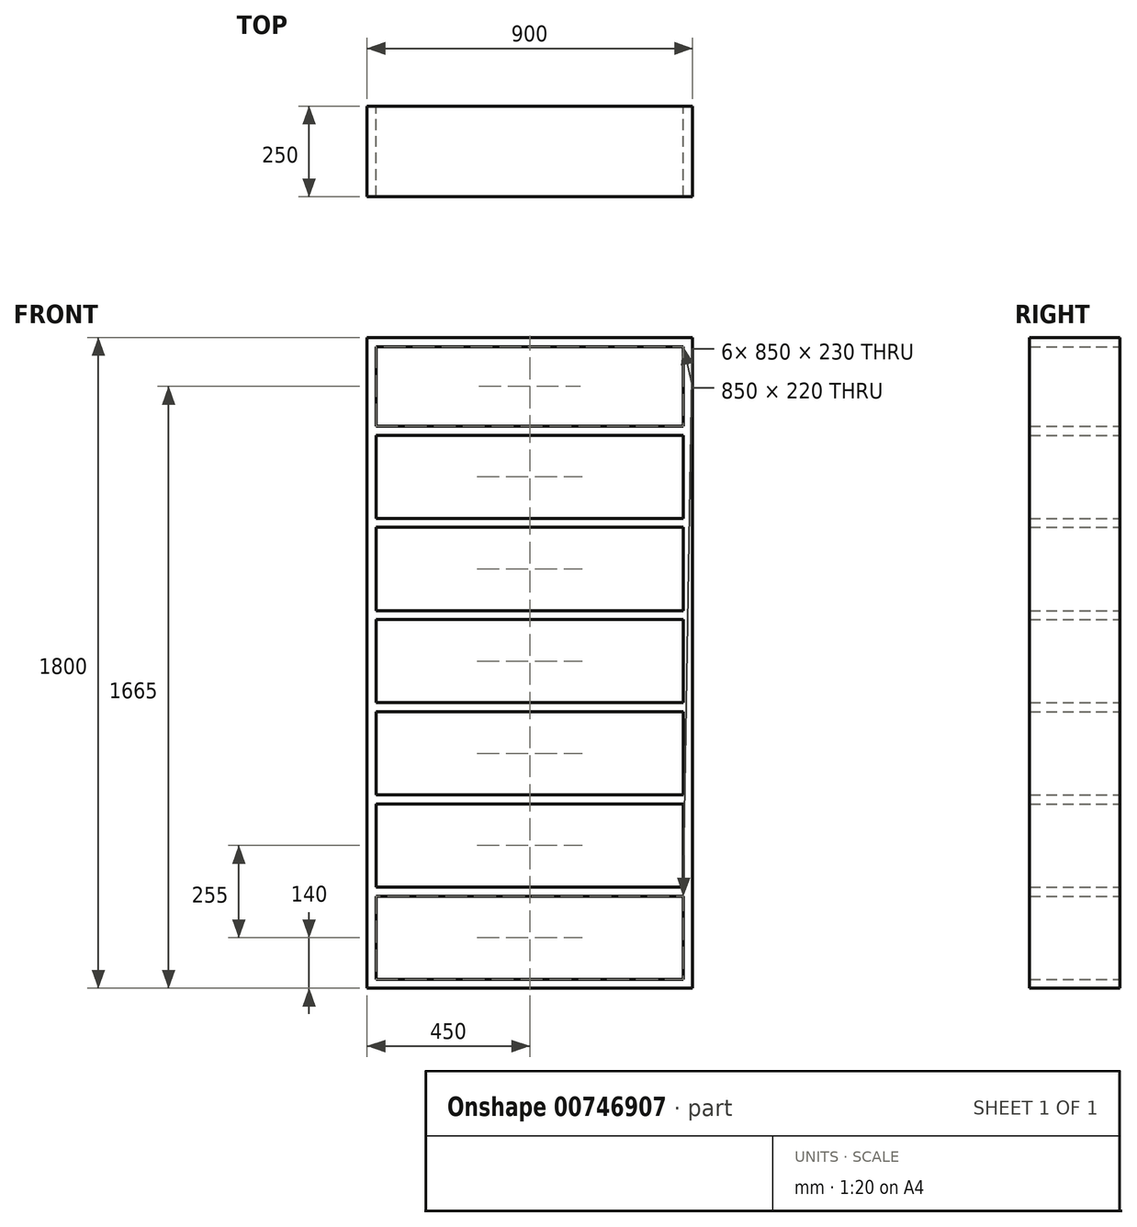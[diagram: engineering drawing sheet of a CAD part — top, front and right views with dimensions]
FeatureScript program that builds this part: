
annotation { "Feature Type Name" : "Feature", "Feature Type Description" : "" }
export const myFeature = defineFeature(function(context is Context, id is Id, definition is map)
    precondition{}
    {
        {
            var Q0;
            Q0=qCreatedBy(makeId("Front.planeOp"),FACE);
            var sketch = newSketch(context, id + "F0", { "sketchPlane" : qUnion([Q0])});
            skLineSegment(sketch, "E0.bottom", {"start": v(450, 0) * mm, "end": v(-450, 0) * mm});
            skLineSegment(sketch, "E0.top", {"start": v(450, 1800) * mm, "end": v(-450, 1800) * mm});
            skLineSegment(sketch, "E0.left", {"start": v(450, 1800) * mm, "end": v(450, 0) * mm});
            skLineSegment(sketch, "E0.right", {"start": v(-450, 1800) * mm, "end": v(-450, 0) * mm});
            skLineSegment(sketch, "E1", {"start": v(0, 1800) * mm, "end": v(0, 0) * mm, "construction": true});
            skLineSegment(sketch, "E2.0", {"start": v(425, 1775) * mm, "end": v(425, 25) * mm});
            skLineSegment(sketch, "E2.1", {"start": v(425, 1775) * mm, "end": v(-425, 1775) * mm});
            skLineSegment(sketch, "E2.2", {"start": v(-425, 1775) * mm, "end": v(-425, 25) * mm});
            skLineSegment(sketch, "E2.3", {"start": v(425, 25) * mm, "end": v(-425, 25) * mm});
            skLineSegment(sketch, "E3.0.1.0", {"start": v(450, 255) * mm, "end": v(-450, 255) * mm});
            skLineSegment(sketch, "E3.0.1.1", {"start": v(425, 280) * mm, "end": v(-425, 280) * mm});
            skLineSegment(sketch, "E3.0.2.0", {"start": v(450, 510) * mm, "end": v(-450, 510) * mm});
            skLineSegment(sketch, "E3.0.2.1", {"start": v(425, 535) * mm, "end": v(-425, 535) * mm});
            skLineSegment(sketch, "E3.0.3.0", {"start": v(450, 765) * mm, "end": v(-450, 765) * mm});
            skLineSegment(sketch, "E3.0.3.1", {"start": v(425, 790) * mm, "end": v(-425, 790) * mm});
            skLineSegment(sketch, "E3.0.4.0", {"start": v(450, 1020) * mm, "end": v(-450, 1020) * mm});
            skLineSegment(sketch, "E3.0.4.1", {"start": v(425, 1045) * mm, "end": v(-425, 1045) * mm});
            skLineSegment(sketch, "E3.0.5.0", {"start": v(450, 1275) * mm, "end": v(-450, 1275) * mm});
            skLineSegment(sketch, "E3.0.5.1", {"start": v(425, 1300) * mm, "end": v(-425, 1300) * mm});
            skLineSegment(sketch, "E3.0.6.0", {"start": v(450, 1530) * mm, "end": v(-450, 1530) * mm});
            skLineSegment(sketch, "E3.0.6.1", {"start": v(425, 1555) * mm, "end": v(-425, 1555) * mm});
            skLineSegment(sketch, "E3.direction1", {"start": v(-450, 0) * mm, "end": v(-425, 0) * mm, "construction": true});
            skLineSegment(sketch, "E3.direction2", {"start": v(-450, 0) * mm, "end": v(-450, 255) * mm, "construction": true});
            skSolve(sketch);
        }
        {
            var Q0;
            Q0 = qSketchRegion(id + "F0", true);
            var Q1;
            {var subQ0=sQuery(id+"F0.wireOp",EDGE,"E3.0.6.1");Q1=makeQuery(id+"F0.imprint","IMPRINT",FACE,{"disambiguationData":[TD([[makeQuery(id+"F0.imprint","IMPRINT",EDGE,{"derivedFrom":subQ0}),1.0]])]});}
            var Q2;
            {var subQ0=sQuery(id+"F0.wireOp",EDGE,"E3.0.5.1");Q2=makeQuery(id+"F0.imprint","IMPRINT",FACE,{"disambiguationData":[TD([[makeQuery(id+"F0.imprint","IMPRINT",EDGE,{"derivedFrom":subQ0}),1.0]])]});}
            var Q3;
            {var subQ0=sQuery(id+"F0.wireOp",EDGE,"E3.0.4.1");Q3=makeQuery(id+"F0.imprint","IMPRINT",FACE,{"disambiguationData":[TD([[makeQuery(id+"F0.imprint","IMPRINT",EDGE,{"derivedFrom":subQ0}),1.0]])]});}
            var Q4;
            {var subQ0=sQuery(id+"F0.wireOp",EDGE,"E3.0.3.1");Q4=makeQuery(id+"F0.imprint","IMPRINT",FACE,{"disambiguationData":[TD([[makeQuery(id+"F0.imprint","IMPRINT",EDGE,{"derivedFrom":subQ0}),1.0]])]});}
            var Q5;
            {var subQ0=sQuery(id+"F0.wireOp",EDGE,"E3.0.2.1");Q5=makeQuery(id+"F0.imprint","IMPRINT",FACE,{"disambiguationData":[TD([[makeQuery(id+"F0.imprint","IMPRINT",EDGE,{"derivedFrom":subQ0}),1.0]])]});}
            var Q6;
            {var subQ0=sQuery(id+"F0.wireOp",EDGE,"E3.0.1.1");Q6=makeQuery(id+"F0.imprint","IMPRINT",FACE,{"disambiguationData":[TD([[makeQuery(id+"F0.imprint","IMPRINT",EDGE,{"derivedFrom":subQ0}),1.0]])]});}
            extrude(context, id + "F1", {"entities" : qUnion([Q0, Q1, Q2, Q3, Q4, Q5, Q6]), "depth" : 250 * mm, "offsetDistance" : 25 * mm});
        }
    });
